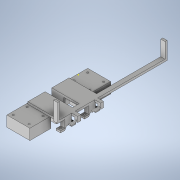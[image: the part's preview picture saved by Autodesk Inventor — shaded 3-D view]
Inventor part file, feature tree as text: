
AUTODESK INVENTOR PART (.ipt)
format: ipt  version: 2020.2 (Build 242310000, 310)  size: 980,992 bytes
history: native  units: mm
features: sketch x36, extrude x36, projected_geometry x19, hole x3
ambient origin geometry x8: Origin, YZ Plane, XZ Plane, XY Plane, X Axis, Y Axis, Z Axis, Center Point
bodies: Solid1 (feature_tree)
feature tree (94):
  sketch  "Sketch1"  dims[d0=8.0mm d1=98.298mm]
  extrude  "Extrusion1"  Depth=98.298mm
  extrude  "Extrusion2"  Depth=4.0mm
  extrude  "Extrusion3"  Depth=4.0mm TaperAngle=0.0deg
  extrude  "Extrusion4"  Depth=34.0mm
  extrude  "Extrusion5"  Depth=12.7mm
  extrude  "Extrusion6"  Depth=25.0mm
  hole  "Hole1"  [1 undecoded]
  extrude  "Extrusion11"  TaperAngle=60.0deg  [1 undecoded]
  extrude  "Extrusion12"  TaperAngle=120.0deg  [1 undecoded]
  sketch  "Sketch16"  dims[d19=6.4262mm d20=120.0deg]
  extrude  "Extrusion13"  Depth=6.4262mm
  extrude  "Extrusion14"  Depth=6.4262mm
  sketch  "Sketch17"  dims[d21=120.0deg d22=6.4262mm]
  extrude  "Extrusion15"  Depth=25.4mm TaperAngle=0.0deg
  extrude  "Extrusion18"  Depth=12.8016mm
  extrude  "Extrusion19"  Depth=12.8016mm
  extrude  "Extrusion20"  Depth=10.0mm
  hole  "Hole2"  [1 undecoded]
  extrude  "Extrusion21"  Depth=2.0mm
  extrude  "Extrusion22"  Depth=2.0mm
  sketch  "Sketch27"  dims[d45=12.8016mm d46=2.0mm]
  extrude  "Extrusion23"  Depth=25.4mm
  extrude  "Extrusion24"  Depth=32.48mm
  extrude  "Extrusion25"  TaperAngle=90.0deg  [1 undecoded]
  sketch  "Sketch29"  dims[d79=51.53mm d80=32.48mm]
  extrude  "Extrusion26"  Depth=2.0mm
  extrude  "Extrusion27"  Depth=21.0mm
  extrude  "Extrusion28"  Depth=36.0mm TaperAngle=0.0deg
  extrude  "Extrusion29"  Depth=8.0mm
  extrude  "Extrusion30"  Depth=17.5mm
  extrude  "Extrusion32"  Depth=35.0mm
  extrude  "Extrusion38"  Depth=5.0mm
  extrude  "Extrusion39"  TaperAngle=90.0deg  [1 undecoded]
  extrude  "Extrusion40"  Depth=5.0mm
  hole  "Hole4"  [1 undecoded]
  extrude  "Extrusion43"  Depth=1.5mm
  extrude  "Extrusion44"  TaperAngle=0.0deg  [1 undecoded]
  extrude  "Extrusion45"  Depth=28.8036mm
  extrude  "Extrusion46"  Depth=25.4mm
  extrude  "Extrusion47"  TaperAngle=120.0deg  [1 undecoded]
  extrude  "Extrusion48"  Depth=12.7mm
  extrude  "Extrusion49"  Depth=12.7mm
  extrude  "Extrusion50"  TaperAngle=120.0deg  [1 undecoded]
  sketch  "Sketch2"  dims[d2=8.0mm d3=4.0mm]
  sketch  "Sketch3"  dims[d4=4.0mm d5=4.0mm d6=0.0mm]
  sketch  "Sketch4"  dims[d7=34.0mm d8=0.0mm d9=19.558mm]
  sketch  "Sketch5"  dims[d10=16.1125mm d11=12.7mm]
  sketch  "Sketch6"  dims[d12=25.0mm d13=0.0mm d14=7.2009mm]
  sketch  "Sketch14"  dims[d15=6.4135mm d16=12.827mm]
  projected_geometry  "Projected Loop2"
  sketch  "Sketch15"  dims[d17=6.4262mm d18=60.0deg]
  projected_geometry  "Projected Loop3"
  sketch  "Sketch18"  dims[d23=120.0deg d24=6.4262mm]
  sketch  "Sketch21"  dims[d25=120.0deg d26=25.4mm d27=0.0mm]
  sketch  "Sketch22"  dims[d28=6.0mm d29=12.8016mm]
  sketch  "Sketch23"  dims[d30=5.9944mm d31=12.8016mm]
  sketch  "Sketch24"  dims[d32=25.4mm d33=0.0mm d34=10.0mm]
  sketch  "Sketch25"  dims[d35=90.0deg d36=20.0mm]
  projected_geometry  "Projected Loop5"
  sketch  "Sketch26"  dims[d37=3.4mm d38=19.05mm d39=6.2992mm d40=6.35mm d41=90.0deg d42=5.0mm d43=0.0mm d44=2.0mm]
  sketch  "Sketch28"  dims[d47=25.4mm d48=0.0mm d78=16.24mm]
  sketch  "Sketch30"  dims[d81=90.0deg d82=90.0deg]
  sketch  "Sketch32"  dims[d83=4.0mm d84=0.0mm d87=2.0mm]
  projected_geometry  "Projected Loop6"
  sketch  "Sketch33"  dims[d88=2.0mm d89=21.0mm]
  projected_geometry  "Projected Loop7"
  sketch  "Sketch35"  dims[d90=2.0mm d91=36.0mm d92=0.0mm]
  projected_geometry  "Projected Loop8"
  sketch  "Sketch42"  dims[d93=17.78mm d94=8.0mm]
  sketch  "Sketch43"  dims[d95=180.0deg d96=17.5mm]
  projected_geometry  "Projected Loop9"
  projected_geometry  "Projected Loop10"
  projected_geometry  "Projected Loop11"
  projected_geometry  "Projected Loop12"
  sketch  "Sketch44"  dims[d97=90.0deg d98=35.0mm]
  sketch  "Sketch45"  dims[d99=3.5mm d100=5.0mm]
  sketch  "Sketch48"  dims[d101=7.0mm d102=90.0deg]
  sketch  "Sketch49"  dims[d103=5.0mm d104=3.4mm]
  projected_geometry  "Projected Loop13"
  projected_geometry  "Projected Loop14"
  sketch  "Sketch50"  dims[d105=3.4mm d106=25.4mm d107=0.0mm]
  projected_geometry  "Projected Loop15"
  sketch  "Sketch51"  dims[d108=6.4262mm d109=0.0mm d110=1.5mm]
  sketch  "Sketch52"  dims[d111=1.5mm d112=0.0mm d113=0.0mm]
  sketch  "Sketch53"  dims[d128=44.8mm d129=28.8036mm]
  projected_geometry  "Projected Loop16"
  projected_geometry  "Projected Loop17"
  projected_geometry  "Projected Loop18"
  projected_geometry  "Projected Loop19"
  sketch  "Sketch54"  dims[d130=25.4mm d131=0.0mm d132=3.2131mm]
  sketch  "Sketch55"  dims[d133=6.4262mm d134=120.0deg d135=3.2131mm d136=6.4262mm d137=120.0deg d138=25.4mm d139=0.0mm d140=8.001mm d141=17.78mm d142=8.001mm d143=0.0mm d144=25.4mm d145=0.0mm d146=10.0mm d147=20.0mm d148=3.4mm d149=19.05mm d150=6.2992mm d151=6.35mm d152=90.0deg d153=5.0mm d154=0.0mm d155=16.2433mm d156=32.4866mm d157=51.5366mm d158=4.0mm d159=0.0mm d160=21.0mm d161=2.0mm d162=2.0mm d163=2.0mm d164=2.0mm d165=36.0mm d166=0.0mm d167=7.0mm d168=5.0mm d169=5.0mm d170=17.5mm d171=35.0mm d172=3.4mm d173=3.4mm d174=5.0mm d175=0.0mm d176=5.0mm d177=0.0mm d178=1.5mm d179=1.5mm d180=25.4mm d181=0.0mm d182=19.05mm d183=10.0mm d184=5.08mm d185=4.0mm d186=0.0mm d187=10.0mm d188=0.0mm d189=2.0mm d190=3.0mm d191=25.4mm d192=0.0mm d194=30.0mm d195=0.0mm d196=102.489mm d197=0.0mm d201=11.43mm d202=0.0mm d239=25.4mm d240=0.0mm d241=1.5mm d242=0.0mm d243=39.0mm d244=35.0mm d245=39.0mm d246=35.0mm d247=3.0mm d248=0.0mm d249=5.0mm d250=5.0mm d251=29.7mm d252=26.05mm d253=4.0mm d254=4.0mm d255=29.7mm d256=26.05mm d257=3.4mm d258=19.05mm d259=6.2992mm d260=6.35mm d261=90.0deg d262=25.4mm d263=20.594885mm d271=4.0mm d272=28.4mm d273=0.0mm d274=25.4mm d275=0.0mm d276=3.429mm d277=180.0deg d278=30.0mm d279=0.0mm d280=6.35mm d281=25.4mm d282=0.0mm d283=5.08mm d284=25.4mm d285=0.0mm d286=2.0mm d287=0.0mm d288=12.7mm d289=0.0mm d290=2.0mm d291=42.9956mm d292=37.0012mm d293=37.0012mm d294=2.0mm d295=2.0mm d296=20.0mm d297=0.0mm d298=16.5086mm d299=2.0mm d214=12.7mm d215=0.872665mm d216=12.7mm d217=0.872665mm d228=12.7mm d229=0.872665mm d230=12.7mm d231=0.872665mm]
  projected_geometry  "Projected Loop20"
  projected_geometry  "Projected Loop21"
note: 10 required parameter values undecoded (feature->parameter linkage not recoverable at this tier; creation-order binding heuristic only, values carry confidence <= 0.55)
